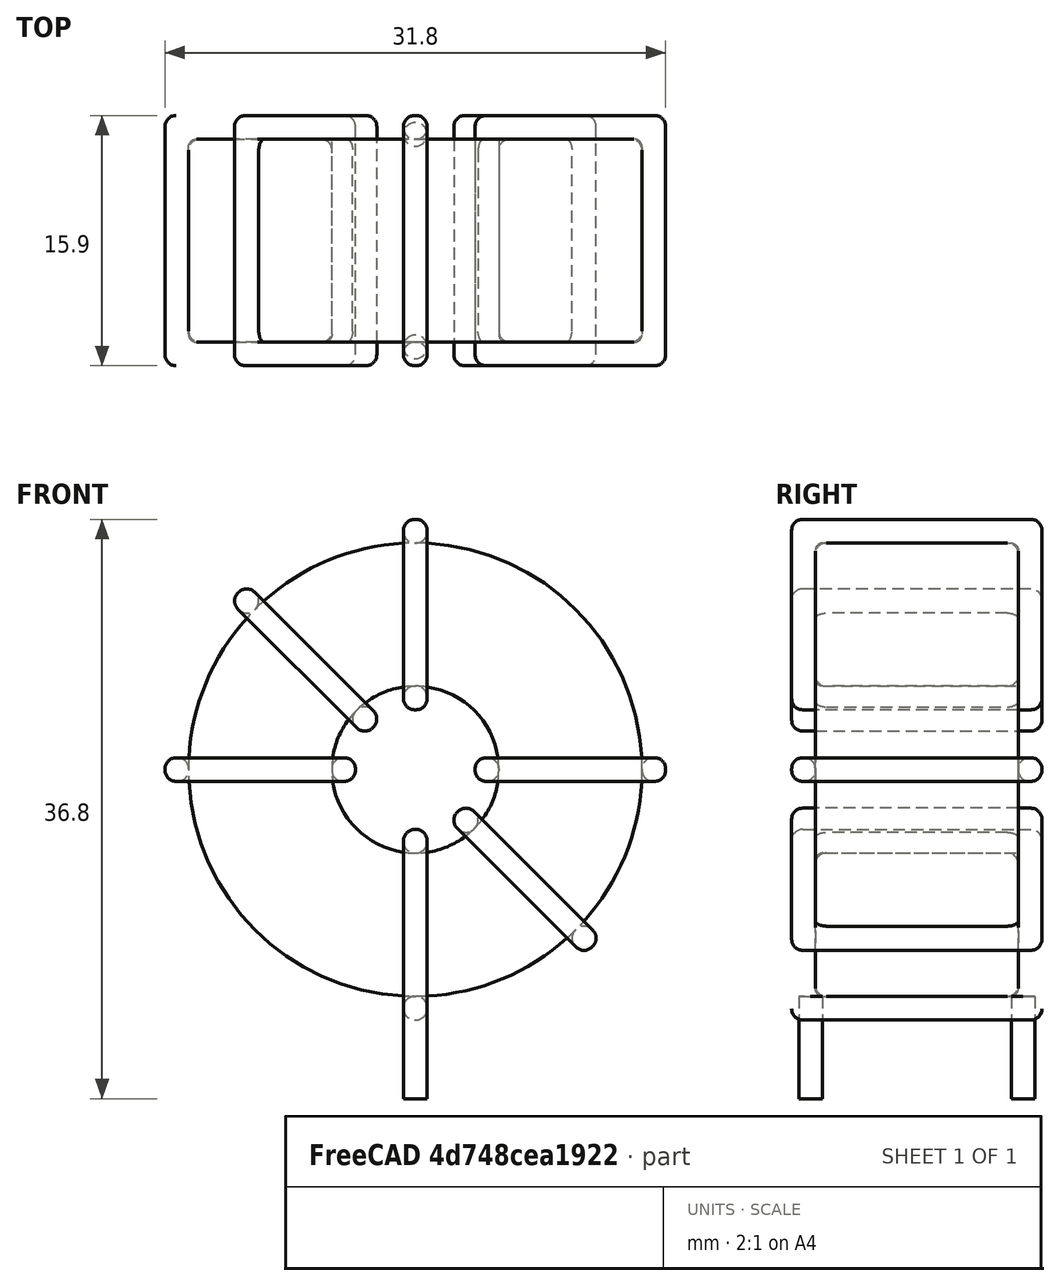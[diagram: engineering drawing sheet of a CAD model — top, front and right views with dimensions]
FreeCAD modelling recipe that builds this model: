
FCSTD DOCUMENT  (FreeCAD 0.16R6703 (Git))
Label: L_Toroid_Vertical_L31.8mm_W15.9mm_P13.50mm_Bourns_5700series
License: All rights reserved
LicenseURL: http://en.wikipedia.org/wiki/All_rights_reserved
objects: Sketcher::SketchObject×6, PartDesign::Pad×6, PartDesign::Fillet×5, Spreadsheet::Sheet×1
note: 23 computed .brp shape members not serialized (recipe doc carries the construction recipe); baked Part::Feature solids carry a one-line shape summary decoded from their .brp

FEATURE [Spreadsheet::Sheet] Spreadsheet  label="dimensions"
  cells = A1=Wx; B1(Wx)=31.8; C1(WW)=10.6; D1=31.8; A2=Wy; B2(Wy)=15.9; D2=15.9; A3=RM; B3(RMx)=13.5; C3(RMy)=0; A4=d_wire; B4(d_wire)=1.5; A5=H; B5(H)=31.8; A6=offsetx; B6(offsetx)=15.9
FEATURE [Sketcher::SketchObject] Sketch
  Placement = pos=(0,-6.75,0) rot=(1,0,0;1.5708rad)
  expr: Placement.Base.y = -Spreadsheet.RMx / 2
  expr: Constraints[0] = Spreadsheet.Wx / 2 - Spreadsheet.d_wire
  expr: Constraints[4] = Spreadsheet.WW / 2
  expr: Constraints[2] = Spreadsheet.Wx / 2 + Spreadsheet.d_wire + 0.5
  sketch-geometry (2):
    g0: Circle CenterX=0 CenterY=17.9 CenterZ=0 NormalX=0 NormalY=0 NormalZ=1 Radius=14.4
    g1: Circle CenterX=0 CenterY=17.9 CenterZ=0 NormalX=0 NormalY=0 NormalZ=1 Radius=5.3
  constraints (5):
    c: Radius(g0) = 14.4
    c: DistanceX(g-1,g0) = 0
    c: DistanceY(g-1,g0) = 17.9
    c: Coincident(g1,g0)
    c: Radius(g1) = 5.3
FEATURE [PartDesign::Pad] Pad
  Length = 12.9
  Length2 = 100
  Midplane = true
  Placement = pos=(0,-6.75,0) rot=(1,0,0;1.5708rad)
  Sketch = -> Sketch
  Type = 0
  expr: Length = Spreadsheet.Wy - 2 * Spreadsheet.d_wire
FEATURE [Sketcher::SketchObject] Sketch001
  Placement = pos=(0,0,2) rot=(0,0,1;0rad)
  expr: Placement.Base.z = 0.5 + Spreadsheet.d_wire
  expr: Constraints[4] = Spreadsheet.RMy
  expr: Constraints[2] = -Spreadsheet.RMx
  expr: Constraints[1] = Spreadsheet.d_wire / 2
  sketch-geometry (2):
    g0: Circle CenterX=0 CenterY=0 CenterZ=0 NormalX=0 NormalY=0 NormalZ=1 Radius=0.75
    g1: Circle CenterX=0 CenterY=-13.5 CenterZ=0 NormalX=0 NormalY=0 NormalZ=1 Radius=0.75
  constraints (5):
    c: Equal(g0,g1)
    c: Radius(g0) = 0.75
    c: DistanceY(g-1,g1) = -13.5
    c: Coincident(g0,g-1)
    c: DistanceX(g-1,g1) = 0
FEATURE [PartDesign::Pad] Pad001
  Length = 1.5
  Length2 = 5
  Placement = pos=(0,0,2) rot=(0,0,1;0rad)
  Reversed = true
  Sketch = -> Sketch001
  Type = 4
  expr: Length2 = 3.5 + Spreadsheet.d_wire
  expr: Length = Spreadsheet.d_wire
FEATURE [PartDesign::Fillet] Fillet
  Base = -> Pad [Edge6,Edge3,Edge2]
  Placement = pos=(0,-6.75,0) rot=(1,0,0;1.5708rad)
  Radius = 0.5
FEATURE [Sketcher::SketchObject] Sketch003
  Placement = pos=(0,1.2,17.9) rot=(1,0,0;3.14159rad)
  expr: Constraints[18] = Spreadsheet.d_wire
  expr: Constraints[16] = Spreadsheet.d_wire
  expr: Constraints[19] = Spreadsheet.d_wire
  expr: Constraints[17] = Spreadsheet.d_wire
  expr: Placement.Base.y = -1 * (Spreadsheet.RMx - Spreadsheet.Wy) / 2
  expr: Constraints[21] = (Spreadsheet.Wx - Spreadsheet.WW) / 2 - Spreadsheet.d_wire
  expr: Constraints[22] = Spreadsheet.Wx / 2 - Spreadsheet.d_wire
  expr: Constraints[43] = Spreadsheet.d_wire
  expr: Constraints[48] = Spreadsheet.Wx - Spreadsheet.d_wire * 2
  expr: Constraints[49] = Spreadsheet.Wy
  expr: Placement.Base.z = Spreadsheet.Wx / 2 + Spreadsheet.d_wire + 0.5
  sketch-geometry (16):
    g0: LineSegment StartX=-3.8 StartY=0 StartZ=0 EndX=-15.9 EndY=0 EndZ=0
    g1: LineSegment StartX=-15.9 StartY=0 StartZ=0 EndX=-15.9 EndY=15.9 EndZ=0
    g2: LineSegment StartX=-15.9 StartY=15.9 StartZ=0 EndX=-3.8 EndY=15.9 EndZ=0
    g3: LineSegment StartX=-3.8 StartY=15.9 StartZ=0 EndX=-3.8 EndY=0 EndZ=0
    g4: LineSegment StartX=-14.4 StartY=14.4 StartZ=0 EndX=-5.3 EndY=14.4 EndZ=0
    g5: LineSegment StartX=-5.3 StartY=14.4 StartZ=0 EndX=-5.3 EndY=1.5 EndZ=0
    g6: LineSegment StartX=-5.3 StartY=1.5 StartZ=0 EndX=-14.4 EndY=1.5 EndZ=0
    g7: LineSegment StartX=-14.4 StartY=1.5 StartZ=0 EndX=-14.4 EndY=14.4 EndZ=0
    g8: LineSegment StartX=3.8 StartY=15.9 StartZ=0 EndX=15.9 EndY=15.9 EndZ=0
    g9: LineSegment StartX=15.9 StartY=15.9 StartZ=0 EndX=15.9 EndY=0 EndZ=0
    g10: LineSegment StartX=15.9 StartY=0 StartZ=0 EndX=3.8 EndY=0 EndZ=0
    g11: LineSegment StartX=3.8 StartY=0 StartZ=0 EndX=3.8 EndY=15.9 EndZ=0
    g12: LineSegment StartX=5.3 StartY=14.4 StartZ=0 EndX=14.4 EndY=14.4 EndZ=0
    g13: LineSegment StartX=14.4 StartY=14.4 StartZ=0 EndX=14.4 EndY=1.5 EndZ=0
    g14: LineSegment StartX=14.4 StartY=1.5 StartZ=0 EndX=5.3 EndY=1.5 EndZ=0
    g15: LineSegment StartX=5.3 StartY=1.5 StartZ=0 EndX=5.3 EndY=14.4 EndZ=0
  constraints (50):
    c: Horizontal(g0)
    c: Coincident(g1,g0)
    c: Vertical(g1)
    c: Coincident(g2,g1)
    c: Horizontal(g2)
    c: Coincident(g3,g2)
    c: Coincident(g3,g0)
    c: Vertical(g3)
    c: Coincident(g4,g5)
    c: Coincident(g5,g6)
    c: Coincident(g6,g7)
    c: Coincident(g7,g4)
    c: Horizontal(g4)
    c: Horizontal(g6)
    c: Vertical(g5)
    c: Vertical(g7)
    c: DistanceX(g1,g4) = 1.5
    c: DistanceY(g4,g1) = 1.5
    c: DistanceX(g5,g0) = 1.5
    c: DistanceY(g0,g5) = 1.5
    c: DistanceY(g-1,g0) = 0
    c: DistanceX(g6,g6) = 9.1
    c: DistanceX(g6,g-1) = 14.4
    c: Coincident(g8,g9)
    c: Coincident(g9,g10)
    c: Coincident(g10,g11)
    c: Coincident(g11,g8)
    c: Horizontal(g8)
    c: Horizontal(g10)
    c: Vertical(g9)
    c: Vertical(g11)
    c: Coincident(g12,g13)
    c: Coincident(g13,g14)
    c: Coincident(g14,g15)
    c: Coincident(g15,g12)
    c: Horizontal(g12)
    c: Horizontal(g14)
    c: Vertical(g13)
    c: Vertical(g15)
    c: DistanceY(g8,g2) = 0
    c: DistanceY(g10,g0) = 0
    c: DistanceY(g14,g5) = 0
    c: DistanceY(g12,g4) = 0
    c: DistanceX(g8,g12) = 1.5
    c: Equal(g8,g2)
    c: Equal(g12,g4)
    c: Equal(g9,g1)
    c: Equal(g13,g7)
    c: DistanceX(g4,g12) = 28.8
    c: DistanceY(g0,g1) = 15.9
FEATURE [PartDesign::Pad] Pad002
  Length = 1.5
  Length2 = 100
  Midplane = true
  Placement = pos=(0,1.2,17.9) rot=(1,0,0;3.14159rad)
  Sketch = -> Sketch003
  Type = 0
  expr: Length = Spreadsheet.d_wire
FEATURE [PartDesign::Fillet] Fillet001
  Base = -> Pad002 [Edge38,Edge41,Edge42,Edge43,Edge29,Edge32,Edge33,Edge34,Edge25,Edge35,Edge36,Edge13,Edge14,Edge15,Edge16,Edge17,Edge18,Edge19,Edge1,Edge2,Edge3,Edge4,Edge5,Edge6,Edge7,Edge37,Edge39,Edge40,Edge20,Edge23,Edge24,Edge21,Edge22,Edge8,Edge9,Edge10,Edge11,Edge12,Edge26,Edge27,+8 more]
  Placement = pos=(0,1.2,17.9) rot=(1,0,0;3.14159rad)
  Radius = 0.705
  expr: Radius = Spreadsheet.d_wire * 0.47
FEATURE [Sketcher::SketchObject] Sketch004
  Placement = pos=(0,1.2,17.9) rot=(0.92388,0,0.382683;3.14159rad)
  expr: Constraints[18] = Spreadsheet.d_wire
  expr: Constraints[16] = Spreadsheet.d_wire
  expr: Constraints[19] = Spreadsheet.d_wire
  expr: Constraints[17] = Spreadsheet.d_wire
  expr: Placement.Base.y = -1 * (Spreadsheet.RMx - Spreadsheet.Wy) / 2
  expr: Constraints[21] = (Spreadsheet.Wx - Spreadsheet.WW) / 2 - Spreadsheet.d_wire
  expr: Constraints[22] = Spreadsheet.Wx / 2 - Spreadsheet.d_wire
  expr: Constraints[43] = Spreadsheet.d_wire
  expr: Constraints[48] = Spreadsheet.Wx - 2 * Spreadsheet.d_wire
  expr: Constraints[49] = Spreadsheet.Wy
  expr: Placement.Base.z = Spreadsheet.Wx / 2 + Spreadsheet.d_wire + 0.5
  sketch-geometry (16):
    g0: LineSegment StartX=-3.8 StartY=0 StartZ=0 EndX=-15.9 EndY=0 EndZ=0
    g1: LineSegment StartX=-15.9 StartY=0 StartZ=0 EndX=-15.9 EndY=15.9 EndZ=0
    g2: LineSegment StartX=-15.9 StartY=15.9 StartZ=0 EndX=-3.8 EndY=15.9 EndZ=0
    g3: LineSegment StartX=-3.8 StartY=15.9 StartZ=0 EndX=-3.8 EndY=0 EndZ=0
    g4: LineSegment StartX=-14.4 StartY=14.4 StartZ=0 EndX=-5.3 EndY=14.4 EndZ=0
    g5: LineSegment StartX=-5.3 StartY=14.4 StartZ=0 EndX=-5.3 EndY=1.5 EndZ=0
    g6: LineSegment StartX=-5.3 StartY=1.5 StartZ=0 EndX=-14.4 EndY=1.5 EndZ=0
    g7: LineSegment StartX=-14.4 StartY=1.5 StartZ=0 EndX=-14.4 EndY=14.4 EndZ=0
    g8: LineSegment StartX=3.8 StartY=15.9 StartZ=0 EndX=15.9 EndY=15.9 EndZ=0
    g9: LineSegment StartX=15.9 StartY=15.9 StartZ=0 EndX=15.9 EndY=0 EndZ=0
    g10: LineSegment StartX=15.9 StartY=0 StartZ=0 EndX=3.8 EndY=0 EndZ=0
    g11: LineSegment StartX=3.8 StartY=0 StartZ=0 EndX=3.8 EndY=15.9 EndZ=0
    g12: LineSegment StartX=5.3 StartY=14.4 StartZ=0 EndX=14.4 EndY=14.4 EndZ=0
    g13: LineSegment StartX=14.4 StartY=14.4 StartZ=0 EndX=14.4 EndY=1.5 EndZ=0
    g14: LineSegment StartX=14.4 StartY=1.5 StartZ=0 EndX=5.3 EndY=1.5 EndZ=0
    g15: LineSegment StartX=5.3 StartY=1.5 StartZ=0 EndX=5.3 EndY=14.4 EndZ=0
  constraints (50):
    c: Horizontal(g0)
    c: Coincident(g1,g0)
    c: Vertical(g1)
    c: Coincident(g2,g1)
    c: Horizontal(g2)
    c: Coincident(g3,g2)
    c: Coincident(g3,g0)
    c: Vertical(g3)
    c: Coincident(g4,g5)
    c: Coincident(g5,g6)
    c: Coincident(g6,g7)
    c: Coincident(g7,g4)
    c: Horizontal(g4)
    c: Horizontal(g6)
    c: Vertical(g5)
    c: Vertical(g7)
    c: DistanceX(g1,g4) = 1.5
    c: DistanceY(g4,g1) = 1.5
    c: DistanceX(g5,g0) = 1.5
    c: DistanceY(g0,g5) = 1.5
    c: DistanceY(g-1,g0) = 0
    c: DistanceX(g6,g6) = 9.1
    c: DistanceX(g6,g-1) = 14.4
    c: Coincident(g8,g9)
    c: Coincident(g9,g10)
    c: Coincident(g10,g11)
    c: Coincident(g11,g8)
    c: Horizontal(g8)
    c: Horizontal(g10)
    c: Vertical(g9)
    c: Vertical(g11)
    c: Coincident(g12,g13)
    c: Coincident(g13,g14)
    c: Coincident(g14,g15)
    c: Coincident(g15,g12)
    c: Horizontal(g12)
    c: Horizontal(g14)
    c: Vertical(g13)
    c: Vertical(g15)
    c: DistanceY(g8,g2) = 0
    c: DistanceY(g10,g0) = 0
    c: DistanceY(g14,g5) = 0
    c: DistanceY(g12,g4) = 0
    c: DistanceX(g8,g12) = 1.5
    c: Equal(g8,g2)
    c: Equal(g12,g4)
    c: Equal(g9,g1)
    c: Equal(g13,g7)
    c: DistanceX(g4,g12) = 28.8
    c: DistanceY(g0,g1) = 15.9
FEATURE [PartDesign::Pad] Pad003
  Length = 1.5
  Length2 = 100
  Midplane = true
  Placement = pos=(0,1.2,17.9) rot=(0.92388,0,0.382683;3.14159rad)
  Sketch = -> Sketch004
  Type = 0
  expr: Length = Spreadsheet.d_wire
FEATURE [PartDesign::Fillet] Fillet002
  Base = -> Pad003 [Edge38,Edge41,Edge42,Edge43,Edge29,Edge32,Edge33,Edge34,Edge25,Edge35,Edge36,Edge13,Edge14,Edge15,Edge16,Edge17,Edge18,Edge19,Edge1,Edge2,Edge3,Edge4,Edge5,Edge6,Edge7,Edge37,Edge39,Edge40,Edge20,Edge23,Edge24,Edge21,Edge22,Edge8,Edge9,Edge10,Edge11,Edge12,Edge26,Edge27,+8 more]
  Placement = pos=(0,1.2,17.9) rot=(0.92388,0,0.382683;3.14159rad)
  Radius = 0.705
  expr: Radius = Spreadsheet.d_wire * 0.47
FEATURE [Sketcher::SketchObject] Sketch005
  Placement = pos=(0,1.2,17.9) rot=(0.92388,0,-0.382683;3.14159rad)
  expr: Constraints[18] = Spreadsheet.d_wire
  expr: Constraints[16] = Spreadsheet.d_wire
  expr: Constraints[19] = Spreadsheet.d_wire
  expr: Constraints[17] = Spreadsheet.d_wire
  expr: Placement.Base.y = -1 * (Spreadsheet.RMx - Spreadsheet.Wy) / 2
  expr: Constraints[21] = (Spreadsheet.Wx - Spreadsheet.WW) / 2 - Spreadsheet.d_wire
  expr: Constraints[22] = Spreadsheet.Wx / 2 - Spreadsheet.d_wire
  expr: Constraints[43] = Spreadsheet.d_wire
  expr: Constraints[48] = Spreadsheet.Wx - 2 * Spreadsheet.d_wire
  expr: Constraints[49] = Spreadsheet.Wy
  expr: Placement.Base.z = Spreadsheet.Wx / 2 + Spreadsheet.d_wire + 0.5
  sketch-geometry (16):
    g0: LineSegment StartX=-3.8 StartY=0 StartZ=0 EndX=-15.9 EndY=0 EndZ=0
    g1: LineSegment StartX=-15.9 StartY=0 StartZ=0 EndX=-15.9 EndY=15.9 EndZ=0
    g2: LineSegment StartX=-15.9 StartY=15.9 StartZ=0 EndX=-3.8 EndY=15.9 EndZ=0
    g3: LineSegment StartX=-3.8 StartY=15.9 StartZ=0 EndX=-3.8 EndY=0 EndZ=0
    g4: LineSegment StartX=-14.4 StartY=14.4 StartZ=0 EndX=-5.3 EndY=14.4 EndZ=0
    g5: LineSegment StartX=-5.3 StartY=14.4 StartZ=0 EndX=-5.3 EndY=1.5 EndZ=0
    g6: LineSegment StartX=-5.3 StartY=1.5 StartZ=0 EndX=-14.4 EndY=1.5 EndZ=0
    g7: LineSegment StartX=-14.4 StartY=1.5 StartZ=0 EndX=-14.4 EndY=14.4 EndZ=0
    g8: LineSegment StartX=3.8 StartY=15.9 StartZ=0 EndX=15.9 EndY=15.9 EndZ=0
    g9: LineSegment StartX=15.9 StartY=15.9 StartZ=0 EndX=15.9 EndY=0 EndZ=0
    g10: LineSegment StartX=15.9 StartY=0 StartZ=0 EndX=3.8 EndY=0 EndZ=0
    g11: LineSegment StartX=3.8 StartY=0 StartZ=0 EndX=3.8 EndY=15.9 EndZ=0
    g12: LineSegment StartX=5.3 StartY=14.4 StartZ=0 EndX=14.4 EndY=14.4 EndZ=0
    g13: LineSegment StartX=14.4 StartY=14.4 StartZ=0 EndX=14.4 EndY=1.5 EndZ=0
    g14: LineSegment StartX=14.4 StartY=1.5 StartZ=0 EndX=5.3 EndY=1.5 EndZ=0
    g15: LineSegment StartX=5.3 StartY=1.5 StartZ=0 EndX=5.3 EndY=14.4 EndZ=0
  constraints (50):
    c: Horizontal(g0)
    c: Coincident(g1,g0)
    c: Vertical(g1)
    c: Coincident(g2,g1)
    c: Horizontal(g2)
    c: Coincident(g3,g2)
    c: Coincident(g3,g0)
    c: Vertical(g3)
    c: Coincident(g4,g5)
    c: Coincident(g5,g6)
    c: Coincident(g6,g7)
    c: Coincident(g7,g4)
    c: Horizontal(g4)
    c: Horizontal(g6)
    c: Vertical(g5)
    c: Vertical(g7)
    c: DistanceX(g1,g4) = 1.5
    c: DistanceY(g4,g1) = 1.5
    c: DistanceX(g5,g0) = 1.5
    c: DistanceY(g0,g5) = 1.5
    c: DistanceY(g-1,g0) = 0
    c: DistanceX(g6,g6) = 9.1
    c: DistanceX(g6,g-1) = 14.4
    c: Coincident(g8,g9)
    c: Coincident(g9,g10)
    c: Coincident(g10,g11)
    c: Coincident(g11,g8)
    c: Horizontal(g8)
    c: Horizontal(g10)
    c: Vertical(g9)
    c: Vertical(g11)
    c: Coincident(g12,g13)
    c: Coincident(g13,g14)
    c: Coincident(g14,g15)
    c: Coincident(g15,g12)
    c: Horizontal(g12)
    c: Horizontal(g14)
    c: Vertical(g13)
    c: Vertical(g15)
    c: DistanceY(g8,g2) = 0
    c: DistanceY(g10,g0) = 0
    c: DistanceY(g14,g5) = 0
    c: DistanceY(g12,g4) = 0
    c: DistanceX(g8,g12) = 1.5
    c: Equal(g8,g2)
    c: Equal(g12,g4)
    c: Equal(g9,g1)
    c: Equal(g13,g7)
    c: DistanceX(g4,g12) = 28.8
    c: DistanceY(g0,g1) = 15.9
FEATURE [PartDesign::Pad] Pad004
  Length = 1.5
  Length2 = 100
  Midplane = true
  Placement = pos=(0,1.2,17.9) rot=(0.92388,0,-0.382683;3.14159rad)
  Sketch = -> Sketch005
  Type = 0
  expr: Length = Spreadsheet.d_wire
FEATURE [PartDesign::Fillet] Fillet003
  Base = -> Pad004 [Edge38,Edge41,Edge42,Edge43,Edge29,Edge32,Edge33,Edge34,Edge25,Edge35,Edge36,Edge13,Edge14,Edge15,Edge16,Edge17,Edge18,Edge19,Edge1,Edge2,Edge3,Edge4,Edge5,Edge6,Edge7,Edge37,Edge39,Edge40,Edge20,Edge23,Edge24,Edge21,Edge22,Edge8,Edge9,Edge10,Edge11,Edge12,Edge26,Edge27,+8 more]
  Placement = pos=(0,1.2,17.9) rot=(0.92388,0,-0.382683;3.14159rad)
  Radius = 0.705
  expr: Radius = Spreadsheet.d_wire * 0.47
FEATURE [Sketcher::SketchObject] Sketch006
  Placement = pos=(0,1.2,17.9) rot=(0.707107,0,0.707107;3.14159rad)
  expr: Constraints[18] = Spreadsheet.d_wire
  expr: Constraints[16] = Spreadsheet.d_wire
  expr: Constraints[19] = Spreadsheet.d_wire
  expr: Constraints[17] = Spreadsheet.d_wire
  expr: Placement.Base.y = -1 * (Spreadsheet.RMx - Spreadsheet.Wy) / 2
  expr: Constraints[21] = (Spreadsheet.Wx - Spreadsheet.WW) / 2 - Spreadsheet.d_wire
  expr: Constraints[22] = Spreadsheet.Wx / 2 - Spreadsheet.d_wire
  expr: Constraints[43] = Spreadsheet.d_wire
  expr: Constraints[48] = Spreadsheet.Wx - Spreadsheet.d_wire * 2
  expr: Constraints[49] = Spreadsheet.Wy
  expr: Placement.Base.z = Spreadsheet.Wx / 2 + Spreadsheet.d_wire + 0.5
  sketch-geometry (16):
    g0: LineSegment StartX=-3.8 StartY=0 StartZ=0 EndX=-15.9 EndY=0 EndZ=0
    g1: LineSegment StartX=-15.9 StartY=0 StartZ=0 EndX=-15.9 EndY=15.9 EndZ=0
    g2: LineSegment StartX=-15.9 StartY=15.9 StartZ=0 EndX=-3.8 EndY=15.9 EndZ=0
    g3: LineSegment StartX=-3.8 StartY=15.9 StartZ=0 EndX=-3.8 EndY=0 EndZ=0
    g4: LineSegment StartX=-14.4 StartY=14.4 StartZ=0 EndX=-5.3 EndY=14.4 EndZ=0
    g5: LineSegment StartX=-5.3 StartY=14.4 StartZ=0 EndX=-5.3 EndY=1.5 EndZ=0
    g6: LineSegment StartX=-5.3 StartY=1.5 StartZ=0 EndX=-14.4 EndY=1.5 EndZ=0
    g7: LineSegment StartX=-14.4 StartY=1.5 StartZ=0 EndX=-14.4 EndY=14.4 EndZ=0
    g8: LineSegment StartX=3.8 StartY=15.9 StartZ=0 EndX=15.9 EndY=15.9 EndZ=0
    g9: LineSegment StartX=15.9 StartY=15.9 StartZ=0 EndX=15.9 EndY=0 EndZ=0
    g10: LineSegment StartX=15.9 StartY=0 StartZ=0 EndX=3.8 EndY=0 EndZ=0
    g11: LineSegment StartX=3.8 StartY=0 StartZ=0 EndX=3.8 EndY=15.9 EndZ=0
    g12: LineSegment StartX=5.3 StartY=14.4 StartZ=0 EndX=14.4 EndY=14.4 EndZ=0
    g13: LineSegment StartX=14.4 StartY=14.4 StartZ=0 EndX=14.4 EndY=1.5 EndZ=0
    g14: LineSegment StartX=14.4 StartY=1.5 StartZ=0 EndX=5.3 EndY=1.5 EndZ=0
    g15: LineSegment StartX=5.3 StartY=1.5 StartZ=0 EndX=5.3 EndY=14.4 EndZ=0
  constraints (50):
    c: Horizontal(g0)
    c: Coincident(g1,g0)
    c: Vertical(g1)
    c: Coincident(g2,g1)
    c: Horizontal(g2)
    c: Coincident(g3,g2)
    c: Coincident(g3,g0)
    c: Vertical(g3)
    c: Coincident(g4,g5)
    c: Coincident(g5,g6)
    c: Coincident(g6,g7)
    c: Coincident(g7,g4)
    c: Horizontal(g4)
    c: Horizontal(g6)
    c: Vertical(g5)
    c: Vertical(g7)
    c: DistanceX(g1,g4) = 1.5
    c: DistanceY(g4,g1) = 1.5
    c: DistanceX(g5,g0) = 1.5
    c: DistanceY(g0,g5) = 1.5
    c: DistanceY(g-1,g0) = 0
    c: DistanceX(g6,g6) = 9.1
    c: DistanceX(g6,g-1) = 14.4
    c: Coincident(g8,g9)
    c: Coincident(g9,g10)
    c: Coincident(g10,g11)
    c: Coincident(g11,g8)
    c: Horizontal(g8)
    c: Horizontal(g10)
    c: Vertical(g9)
    c: Vertical(g11)
    c: Coincident(g12,g13)
    c: Coincident(g13,g14)
    c: Coincident(g14,g15)
    c: Coincident(g15,g12)
    c: Horizontal(g12)
    c: Horizontal(g14)
    c: Vertical(g13)
    c: Vertical(g15)
    c: DistanceY(g8,g2) = 0
    c: DistanceY(g10,g0) = 0
    c: DistanceY(g14,g5) = 0
    c: DistanceY(g12,g4) = 0
    c: DistanceX(g8,g12) = 1.5
    c: Equal(g8,g2)
    c: Equal(g12,g4)
    c: Equal(g9,g1)
    c: Equal(g13,g7)
    c: DistanceX(g4,g12) = 28.8
    c: DistanceY(g0,g1) = 15.9
FEATURE [PartDesign::Pad] Pad005
  Length = 1.5
  Length2 = 100
  Midplane = true
  Placement = pos=(0,1.2,17.9) rot=(0.707107,0,0.707107;3.14159rad)
  Sketch = -> Sketch006
  Type = 0
  expr: Length = Spreadsheet.d_wire
FEATURE [PartDesign::Fillet] Fillet004
  Base = -> Pad005 [Edge38,Edge41,Edge42,Edge43,Edge29,Edge32,Edge33,Edge34,Edge25,Edge35,Edge36,Edge13,Edge14,Edge15,Edge16,Edge17,Edge18,Edge19,Edge1,Edge2,Edge3,Edge4,Edge5,Edge6,Edge7,Edge37,Edge39,Edge40,Edge20,Edge23,Edge24,Edge21,Edge22,Edge8,Edge9,Edge10,Edge11,Edge12,Edge26,Edge27,+8 more]
  Placement = pos=(0,1.2,17.9) rot=(0.707107,0,0.707107;3.14159rad)
  Radius = 0.705
  expr: Radius = Spreadsheet.d_wire * 0.47
